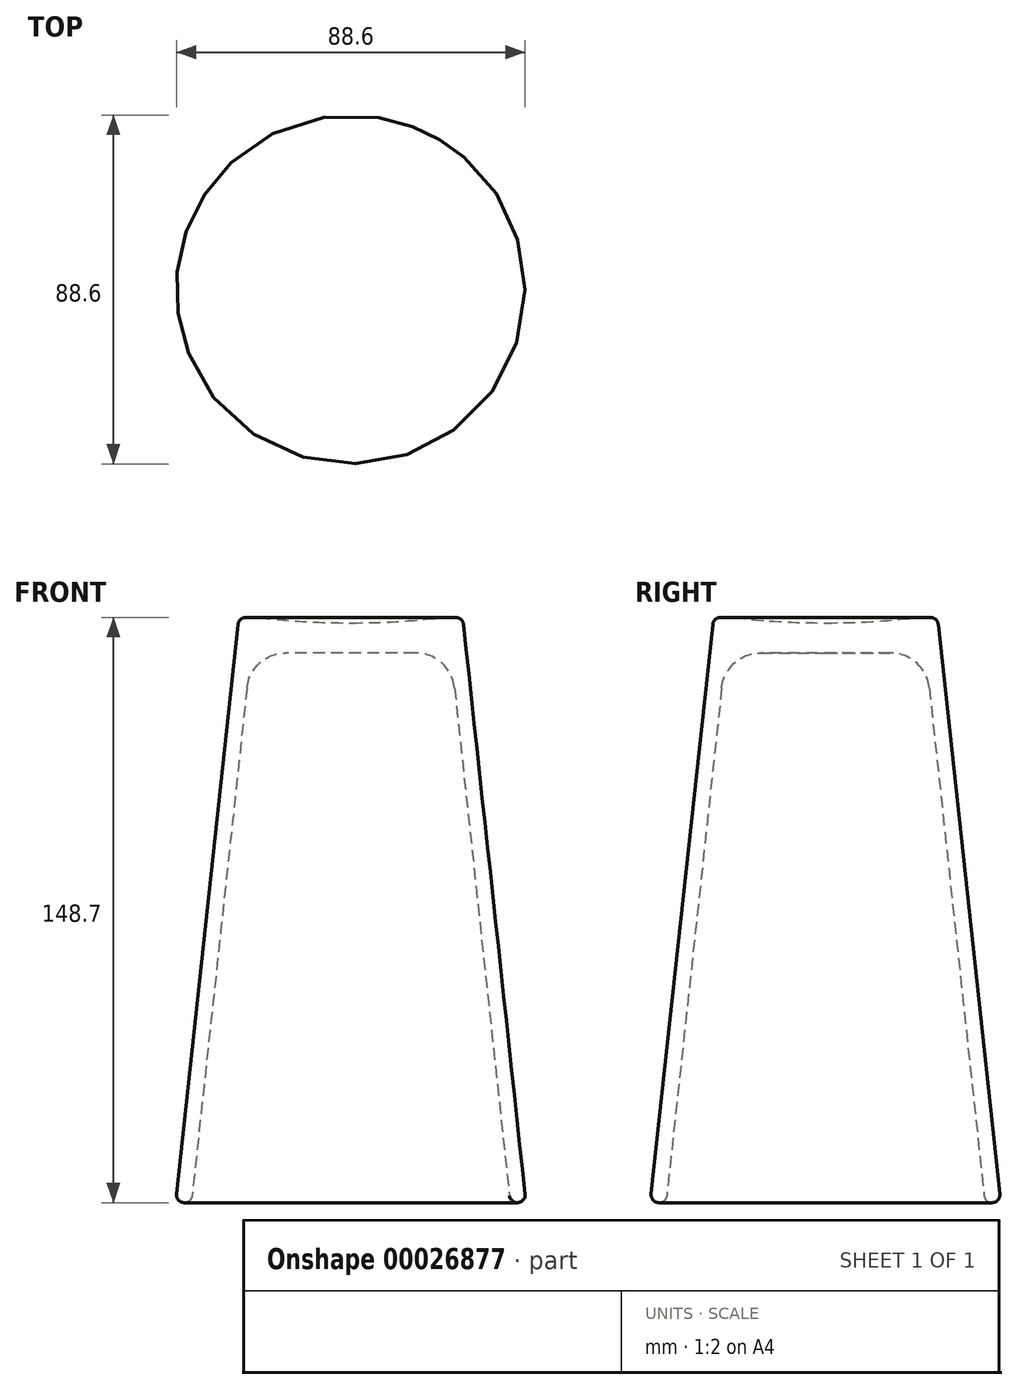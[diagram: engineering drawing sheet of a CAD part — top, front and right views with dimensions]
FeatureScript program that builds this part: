
annotation { "Feature Type Name" : "Feature", "Feature Type Description" : "" }
export const myFeature = defineFeature(function(context is Context, id is Id, definition is map)
    precondition{}
    {
        {
            var Q0;
            Q0=qCreatedBy(makeId("Front.planeOp"),FACE);
            var sketch = newSketch(context, id + "F0", { "sketchPlane" : qUnion([Q0])});
            skLineSegment(sketch, "E0", {"start": v(0, 71.17) * mm, "end": v(0, -48.44) * mm, "construction": true});
            skLineSegment(sketch, "E1", {"start": v(23.45, 0) * mm, "end": v(28.45, 0) * mm});
            skLineSegment(sketch, "E2", {"start": v(28.45, 0) * mm, "end": v(44.52, 148.7) * mm});
            skLineSegment(sketch, "E3", {"start": v(44.52, 148.7) * mm, "end": v(40.5, 148.7) * mm});
            skLineSegment(sketch, "E4", {"start": v(40.5, 148.7) * mm, "end": v(25.4, 9) * mm});
            skLineSegment(sketch, "E5", {"start": v(25.4, 9) * mm, "end": v(0, 9) * mm});
            skLineSegment(sketch, "E6", {"start": v(0, 9) * mm, "end": v(0, 0) * mm});
            skArc(sketch, "E7", {"start": v(23.45, 0) * mm, "mid": v(0, 1.38) * mm, "end": v(-23.45, 0) * mm});
            skSolve(sketch);
        }
        {
            var Q0;
            Q0 = qSketchRegion(id + "F0", true);
            var Q1;
            Q1=sQuery(id+"F0.wireOp",EDGE,"E0");
            revolve(context, id + "F1", {"entities" : qUnion([Q0]), "axis" : qUnion([Q1]), "revolveType" : RevolveType.FULL});
        }
        {
            var Q0;
            Q0=makeQuery(id+"F1.opRevolve","SWEPT_EDGE",EDGE,{"disambiguationData":[OSD([sQuery(id+"F0.wireOp",EDGE,"E1"),sQuery(id+"F0.wireOp",EDGE,"E2")])]});
            var Q1;
            Q1=makeQuery(id+"F1.opRevolve","SWEPT_EDGE",EDGE,{"disambiguationData":[OSD([sQuery(id+"F0.wireOp",EDGE,"E1"),sQuery(id+"F0.wireOp",EDGE,"E7")])]});
            var Q2;
            Q2=makeQuery(id+"F1.opRevolve","SWEPT_EDGE",EDGE,{"disambiguationData":[OSD([sQuery(id+"F0.wireOp",EDGE,"E2"),sQuery(id+"F0.wireOp",EDGE,"E3")])]});
            var Q3;
            Q3=makeQuery(id+"F1.opRevolve","SWEPT_EDGE",EDGE,{"disambiguationData":[OSD([sQuery(id+"F0.wireOp",EDGE,"E3"),sQuery(id+"F0.wireOp",EDGE,"E4")])]});
            fillet(context, id + "F2", {"entities" : qUnion([Q0, Q1, Q2, Q3]), "radius" : 2 * mm, "tangentPropagation" : true, "allowEdgeOverflow" : false});
        }
        {
            var Q0;
            Q0=makeQuery(id+"F1.opRevolve","SWEPT_EDGE",EDGE,{"disambiguationData":[OSD([sQuery(id+"F0.wireOp",EDGE,"E4"),sQuery(id+"F0.wireOp",EDGE,"E5")])]});
            fillet(context, id + "F3", {"entities" : qUnion([Q0]), "radius" : 10 * mm, "tangentPropagation" : true, "allowEdgeOverflow" : false});
        }
        {
            var Q0;
            Q0=makeQuery(id+"F1.opRevolve","SWEPT_BODY",BODY,{"disambiguationData":[OSD([sQuery(id+"F0.wireOp",EDGE,"E1"),sQuery(id+"F0.wireOp",EDGE,"E2"),sQuery(id+"F0.wireOp",EDGE,"E3"),sQuery(id+"F0.wireOp",EDGE,"E4"),sQuery(id+"F0.wireOp",EDGE,"E5"),sQuery(id+"F0.wireOp",EDGE,"E6"),sQuery(id+"F0.wireOp",EDGE,"E7")])]});
            var Q1;
            Q1=sQuery(id+"F0.wireOp",EDGE,"E7");
            transform(context, id + "F4", {"entities" : qUnion([Q0]), "transformType" : TransformType.ROTATION, "transformAxis" : qUnion([Q1]), "angle" : 180 * degree, "makeCopy" : false});
        }
    });
